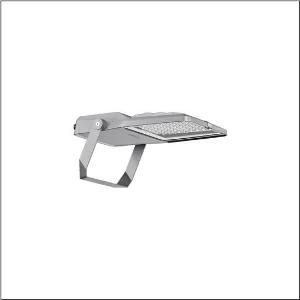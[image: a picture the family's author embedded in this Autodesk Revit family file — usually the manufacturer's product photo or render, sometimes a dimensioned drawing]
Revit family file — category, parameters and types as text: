
# Revit family: floodlight_fl_21_iq_mini___pl52_5xa7772c5d1a_6522
name_source: partatom
category: Lighting Fixtures
units: mm (PartAtom-declared; Revit-internal decimal feet)

## family parameters
Cut with Voids When Loaded = No
Host = Face
Light Source = No
Part Type = Normal
Room Calculation Point = No
Round Connector Dimension = Use Diameter
Shared = No

## types (1)
- --- (1 x LED, 11390 lm, 87.2 W, 4000K)
    Apparent Load = 87 VA
    CIE Flux Codes = 26 60 98 100 100
    Color Rendering = 80
    Color Temperature = 4000K
    Default Elevation = 1800 mm
    Description = Floodlight FL 21 iQ mini, floodlight, primary light control with lens, of PMMA, primary optical cover: protective disc, of toughened safety glass, transparent, light distribution: PL52, light emission: direct distribution, installation type: surface-mounted, LED, High Power LED, rated luminous flux: 11.390lm, luminous efficacy: 131lm/W, light colour: 840, colour temperature: 4000K, control: Street-Remote, Auto-Match, Temp-Guard, Night-Set, Smart-Wire, Desk-Remote (wireless, voltage-free reading and setting of iQ features in the workshop via application-optimized NFC function/RFID function), optimised constant luminous flux control (CLO 2.0), with terminal, 6-pole, mains connection: 220..240V, AC, 50/60Hz, start of lifetime: 87W, end of service life: 92W, reduction: 40W, luminaire housing, of diecast aluminium, powder-coated, Siteco® metallic grey (DB 702S), corrosivity category C5 mid according to DIN EN ISO 12944, sealing non-destructively replaceable, mounting bracket, of steel, galvanised, powder-coated, Siteco® metallic grey (DB 702S), protection rating (complete): IP66, insulation class (complete): insulation class II (safety insulation), certification: CE, ENEC, VDE, protection symbol: D, impact resistance: IK08, permissible operating ambient temperature: -40..+40°C, permissible operating ambient temperature for outdoor applications: -40..+50°C, standard: DIN EN 12944, LABS conformity tested according to VDMA 24364:2018-05, packaging unit: 1 piece

Light Distribution: PL52
    Height = 70 mm
    Lamp = 1 x LED
    Lamp Light Flux = 11390 lm
    Lamp Power = 87.2 W
    Lamp count = 1
    Length = 485 mm
    Luminous efficacy = 131 lm/W
    Manufacturer = Siteco
    ModVariant = No
    Model = 5XA7772C5D1A
    Number of Poles = 1
    OnlyDefault = Yes
    Power Factor = 1
    Product Name = Floodlight FL 21 iQ mini | PL52
    Product group = floodlight | pylon annexe
    ProductGroupID = 6200
    Protection Class = Protection class II
    Protection Degree = IP 66
    RLX_Detail_Level = 1
    RLX_Emergency_Light_Flux = 0 lm
    RLX_Emergency_Type = 0
    RLX_Emergency_Type_DB = No
    RlxData = <blob elided: 96521 chars, md5=d53b44d9>
    Socket = socket
    Standby Power = 0 W
    System Light Flux = 11390 lm
    System Power = 87 W
    Type Comments = factory setting: luminous flux: 100 % | dim-lin: 254 | 456 mA
    Type Image = l_1006845.jpg
    URL = http://relux.com
    VarID = @adj_114275
    Voltage = 0 V
    Weight = 0.00 kg
    Width = 337 mm

## geometry (parser evidence)
native form markers: Blend x4, Sweep x12
no freeform markers — native parametric forms only
